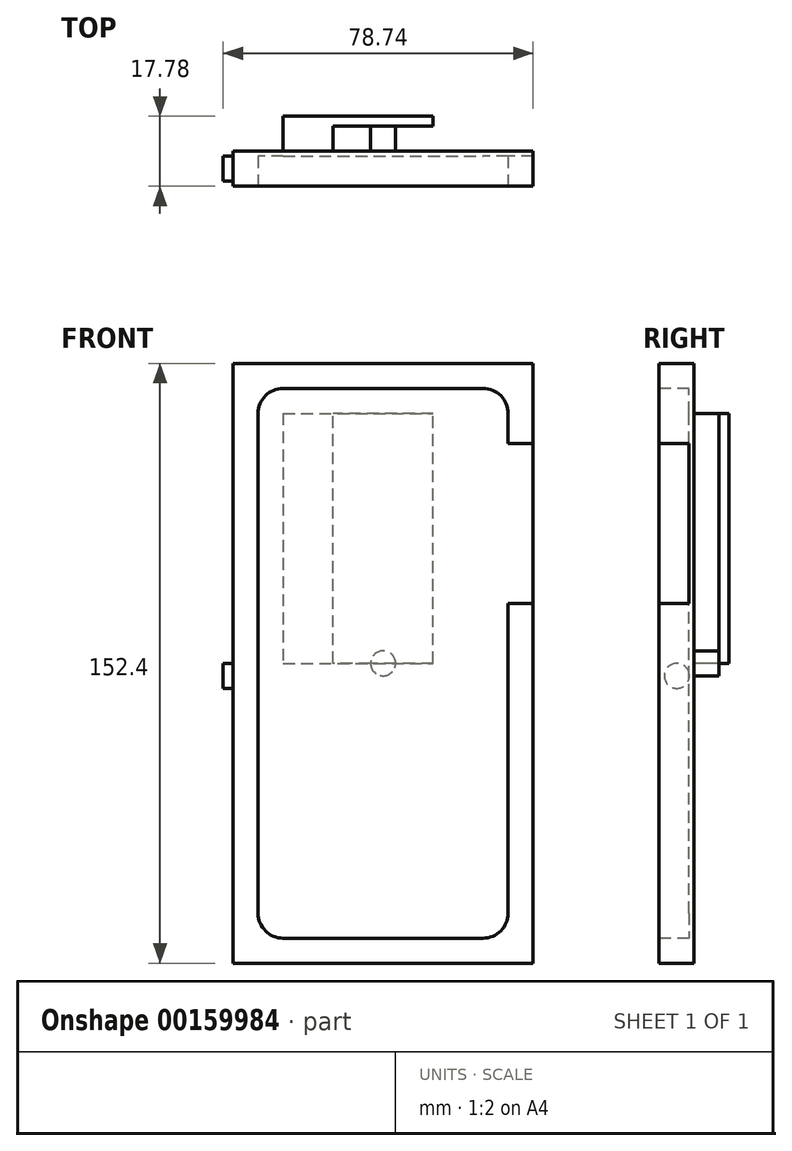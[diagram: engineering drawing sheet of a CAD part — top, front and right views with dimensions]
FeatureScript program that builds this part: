
annotation { "Feature Type Name" : "Feature", "Feature Type Description" : "" }
export const myFeature = defineFeature(function(context is Context, id is Id, definition is map)
    precondition{}
    {
        {
            var Q0;
            Q0=qCreatedBy(makeId("Front.planeOp"),FACE);
            var sketch = newSketch(context, id + "F0", { "sketchPlane" : qUnion([Q0])});
            skLineSegment(sketch, "E0.bottom", {"start": v(0, 6.52) * mm, "end": v(-76.2, 6.52) * mm});
            skLineSegment(sketch, "E0.top", {"start": v(0, 158.92) * mm, "end": v(-76.2, 158.92) * mm});
            skLineSegment(sketch, "E0.left", {"start": v(0, 6.52) * mm, "end": v(0, 158.92) * mm});
            skLineSegment(sketch, "E0.right", {"start": v(-76.2, 6.52) * mm, "end": v(-76.2, 158.92) * mm});
            skSolve(sketch);
        }
        {
            var Q0;
            Q0=makeQuery(id+"F0.imprint","IMPRINT",FACE,{"disambiguationData":[TD([[makeQuery(id+"F0.imprint","IMPRINT",EDGE,{"derivedFrom":sQuery(id+"F0.wireOp",EDGE,"E0.bottom")}),-1.0]])]});
            extrude(context, id + "F1", {"entities" : qUnion([Q0]), "depth" : 8.9 * mm});
        }
        {
            var Q0;
            Q0=makeQuery(id+"F1.opExtrude","CAP_FACE",FACE,{"disambiguationData":[OSD([sQuery(id+"F0.wireOp",EDGE,"E0.bottom"),sQuery(id+"F0.wireOp",EDGE,"E0.top"),sQuery(id+"F0.wireOp",EDGE,"E0.left"),sQuery(id+"F0.wireOp",EDGE,"E0.right")])],"isStart":false});
            var sketch = newSketch(context, id + "F2", { "sketchPlane" : qUnion([Q0])});
            skLineSegment(sketch, "E1.bottom", {"start": v(-63.5, 12.87) * mm, "end": v(-12.7, 12.87) * mm});
            skLineSegment(sketch, "E1.top", {"start": v(-63.5, 152.57) * mm, "end": v(-12.7, 152.57) * mm});
            skLineSegment(sketch, "E1.left", {"start": v(-69.85, 19.22) * mm, "end": v(-69.85, 146.22) * mm});
            skLineSegment(sketch, "E1.right", {"start": v(-6.35, 19.22) * mm, "end": v(-6.35, 146.22) * mm});
            skLineSegment(sketch, "E2", {"start": v(-50.26, 152.57) * mm, "end": v(-50.26, 158.92) * mm});
            skLineSegment(sketch, "E3", {"start": v(-69.85, 115.08) * mm, "end": v(-76.2, 115.08) * mm});
            skPoint(sketch, "E4.end.orphan", {"position": v(-69.85, 157.04) * mm});
            skPoint(sketch, "E5.visualSharp", {"position": v(-69.85, 152.57) * mm});
            skArc(sketch, "E5.filletArc", {"start": v(-63.5, 152.57) * mm, "mid": v(-68, 150.71) * mm, "end": v(-69.85, 146.22) * mm});
            skPoint(sketch, "E6.visualSharp", {"position": v(-6.35, 152.57) * mm});
            skArc(sketch, "E6.filletArc", {"start": v(-6.35, 146.22) * mm, "mid": v(-8.2, 150.71) * mm, "end": v(-12.7, 152.57) * mm});
            skPoint(sketch, "E7.visualSharp", {"position": v(-6.35, 12.87) * mm});
            skArc(sketch, "E7.filletArc", {"start": v(-12.7, 12.87) * mm, "mid": v(-8.2, 14.73) * mm, "end": v(-6.35, 19.22) * mm});
            skPoint(sketch, "E8.visualSharp", {"position": v(-69.85, 12.87) * mm});
            skArc(sketch, "E8.filletArc", {"start": v(-69.85, 19.22) * mm, "mid": v(-68, 14.73) * mm, "end": v(-63.5, 12.87) * mm});
            skSolve(sketch);
        }
        {
            var Q0;
            Q0=makeQuery(id+"F2.imprint","IMPRINT",FACE,{"disambiguationData":[TD([[makeQuery(id+"F2.imprint","IMPRINT",EDGE,{"derivedFrom":sQuery(id+"F2.wireOp",EDGE,"E1.bottom")}),1.0]])]});
            extrude(context, id + "F3", {"entities" : qUnion([Q0]), "operationType" : NewBodyOperationType.REMOVE, "oppositeDirection" : true, "depth" : 7.62 * mm});
        }
        {
            var Q0;
            Q0=makeQuery(id+"F1.opExtrude","CAP_FACE",FACE,{"disambiguationData":[OSD([sQuery(id+"F0.wireOp",EDGE,"E0.bottom"),sQuery(id+"F0.wireOp",EDGE,"E0.top"),sQuery(id+"F0.wireOp",EDGE,"E0.left"),sQuery(id+"F0.wireOp",EDGE,"E0.right")])],"isStart":false});
            var sketch = newSketch(context, id + "F4", { "sketchPlane" : qUnion([Q0])});
            skPoint(sketch, "E9.start.orphan", {"position": v(-3.88, 97.96) * mm});
            skLineSegment(sketch, "E10", {"start": v(0, 158.92) * mm, "end": v(0, 138.6) * mm});
            skLineSegment(sketch, "E11.bottom", {"start": v(0, 138.6) * mm, "end": v(-6.35, 138.6) * mm});
            skLineSegment(sketch, "E11.top", {"start": v(0, 97.96) * mm, "end": v(-6.35, 97.96) * mm});
            skLineSegment(sketch, "E11.left", {"start": v(0, 138.6) * mm, "end": v(0, 97.96) * mm});
            skLineSegment(sketch, "E11.right", {"start": v(-6.35, 138.6) * mm, "end": v(-6.35, 97.96) * mm});
            skSolve(sketch);
        }
        {
            var Q0;
            Q0=makeQuery(id+"F4.imprint","IMPRINT",FACE,{"disambiguationData":[TD([[makeQuery(id+"F4.imprint","IMPRINT",EDGE,{"derivedFrom":sQuery(id+"F4.wireOp",EDGE,"E11.bottom")}),1.0]])]});
            extrude(context, id + "F5", {"entities" : qUnion([Q0]), "operationType" : NewBodyOperationType.REMOVE, "oppositeDirection" : true, "depth" : 7.62 * mm});
        }
        {
            var Q0;
            Q0=makeQuery(id+"F1.opExtrude","SWEPT_FACE",FACE,{"disambiguationData":[OSD([sQuery(id+"F0.wireOp",EDGE,"E0.right")])]});
            var sketch = newSketch(context, id + "F6", { "sketchPlane" : qUnion([Q0])});
            skCircle(sketch, "E12", {"center": v(4.37, 79.55) * mm, "radius": 3.18 * mm});
            skLineSegment(sketch, "E13", {"start": v(4.45, 6.52) * mm, "end": v(4.45, 76.37) * mm});
            skSolve(sketch);
        }
        {
            var Q0;
            Q0=makeQuery(id+"F6.imprint","IMPRINT",FACE,{"disambiguationData":[TD([[makeQuery(id+"F6.imprint","IMPRINT",EDGE,{"derivedFrom":sQuery(id+"F6.wireOp",EDGE,"E12")}),1.0]])]});
            extrude(context, id + "F7", {"entities" : qUnion([Q0]), "operationType" : NewBodyOperationType.REMOVE, "oppositeDirection" : true, "depth" : 2.54 * mm});
        }
        {
            var Q0;
            Q0=makeQuery(id+"F7.boolean.opBoolean","COPY",FACE,{"derivedFrom":makeQuery(id+"F7.opExtrude","CAP_FACE",FACE,{"disambiguationData":[OSD([sQuery(id+"F6.wireOp",EDGE,"E12")])],"isStart":false})});
            extrude(context, id + "F8", {"entities" : qUnion([Q0]), "operationType" : NewBodyOperationType.ADD, "depth" : 5.08 * mm});
        }
        {
            var Q0;
            Q0=makeQuery(id+"F1.opExtrude","CAP_FACE",FACE,{"disambiguationData":[OSD([sQuery(id+"F0.wireOp",EDGE,"E0.bottom"),sQuery(id+"F0.wireOp",EDGE,"E0.top"),sQuery(id+"F0.wireOp",EDGE,"E0.left"),sQuery(id+"F0.wireOp",EDGE,"E0.right")])],"isStart":true});
            var sketch = newSketch(context, id + "F9", { "sketchPlane" : qUnion([Q0])});
            skCircle(sketch, "E14", {"center": v(38.1, 82.72) * mm, "radius": 3.18 * mm});
            skPoint(sketch, "E14.centerSnap0", {"position": v(0, 82.72) * mm});
            skPoint(sketch, "E14.centerSnap1", {"position": v(38.1, 158.92) * mm});
            skSolve(sketch);
        }
        {
            var Q0;
            Q0=makeQuery(id+"F9.imprint","IMPRINT",FACE,{"disambiguationData":[TD([[makeQuery(id+"F9.imprint","IMPRINT",EDGE,{"derivedFrom":sQuery(id+"F9.wireOp",EDGE,"E14")}),1.0]])]});
            extrude(context, id + "F10", {"entities" : qUnion([Q0]), "operationType" : NewBodyOperationType.ADD, "depth" : 6.35 * mm});
        }
        {
            var Q0;
            Q0=makeQuery(id+"F1.opExtrude","CAP_FACE",FACE,{"disambiguationData":[OSD([sQuery(id+"F0.wireOp",EDGE,"E0.bottom"),sQuery(id+"F0.wireOp",EDGE,"E0.top"),sQuery(id+"F0.wireOp",EDGE,"E0.left"),sQuery(id+"F0.wireOp",EDGE,"E0.right")])],"isStart":true});
            var sketch = newSketch(context, id + "F11", { "sketchPlane" : qUnion([Q0])});
            skLineSegment(sketch, "E15.bottom", {"start": v(76.2, 82.72) * mm, "end": v(50.8, 82.72) * mm});
            skLineSegment(sketch, "E15.top", {"start": v(76.2, 146.22) * mm, "end": v(50.8, 146.22) * mm});
            skLineSegment(sketch, "E15.left", {"start": v(76.2, 82.72) * mm, "end": v(76.2, 146.22) * mm});
            skLineSegment(sketch, "E15.right", {"start": v(50.8, 82.72) * mm, "end": v(50.8, 146.22) * mm});
            skLineSegment(sketch, "E16", {"start": v(63.5, 146.22) * mm, "end": v(63.5, 82.72) * mm});
            skSolve(sketch);
        }
        {
            var Q0;
            {var subQ0=sQuery(id+"F11.wireOp",EDGE,"E15.right");Q0=makeQuery(id+"F11.imprint","IMPRINT",FACE,{"disambiguationData":[TD([[makeQuery(id+"F11.imprint","IMPRINT",EDGE,{"derivedFrom":subQ0}),-1.0]])]});}
            extrude(context, id + "F12", {"entities" : qUnion([Q0]), "operationType" : NewBodyOperationType.ADD, "depth" : 8.9 * mm});
        }
        {
            var Q0;
            Q0=makeQuery(id+"F12.opExtrude","SWEPT_FACE",FACE,{"disambiguationData":[OSD([sQuery(id+"F11.wireOp",EDGE,"E15.right")])]});
            var sketch = newSketch(context, id + "F13", { "sketchPlane" : qUnion([Q0])});
            skLineSegment(sketch, "E17.bottom", {"start": v(8.9, 82.72) * mm, "end": v(6.35, 82.72) * mm});
            skLineSegment(sketch, "E17.top", {"start": v(8.9, 146.22) * mm, "end": v(6.35, 146.22) * mm});
            skLineSegment(sketch, "E17.left", {"start": v(8.9, 82.72) * mm, "end": v(8.9, 146.22) * mm});
            skLineSegment(sketch, "E17.right", {"start": v(6.35, 82.72) * mm, "end": v(6.35, 146.22) * mm});
            skSolve(sketch);
        }
        {
            var Q0;
            Q0=makeQuery(id+"F13.imprint","IMPRINT",FACE,{"disambiguationData":[TD([[makeQuery(id+"F13.imprint","IMPRINT",EDGE,{"derivedFrom":sQuery(id+"F13.wireOp",EDGE,"E17.bottom")}),-1.0]])]});
            extrude(context, id + "F14", {"entities" : qUnion([Q0]), "operationType" : NewBodyOperationType.ADD, "depth" : 25.4 * mm});
        }
    });
